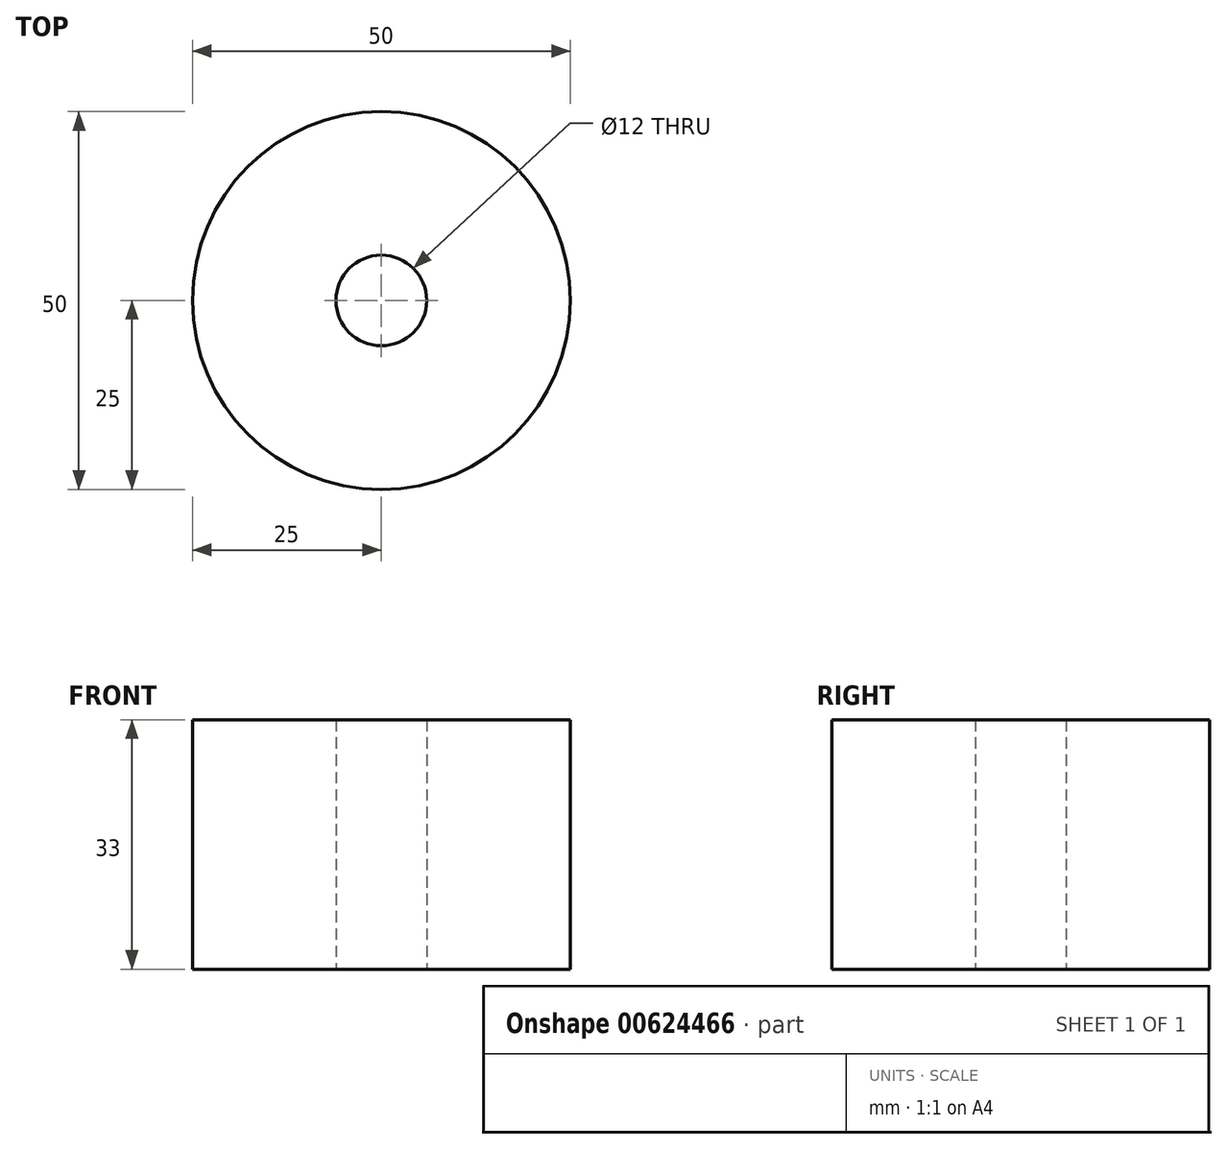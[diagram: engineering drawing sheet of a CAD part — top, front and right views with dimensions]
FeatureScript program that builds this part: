
annotation { "Feature Type Name" : "Feature", "Feature Type Description" : "" }
export const myFeature = defineFeature(function(context is Context, id is Id, definition is map)
    precondition{}
    {
        {
            var Q0;
            Q0=qCreatedBy(makeId("Top.planeOp"),FACE);
            var sketch = newSketch(context, id + "F0", { "sketchPlane" : qUnion([Q0])});
            skCircle(sketch, "E0", {"center": v(0, 0) * mm, "radius": 25 * mm});
            skCircle(sketch, "E1", {"center": v(0, 0) * mm, "radius": 6 * mm});
            skSolve(sketch);
        }
        {
            var Q0;
            Q0 = qSketchRegion(id + "F0", true);
            extrude(context, id + "F1", {"entities" : qUnion([Q0]), "depth" : 33 * mm, "offsetDistance" : 25 * mm});
        }
    });
